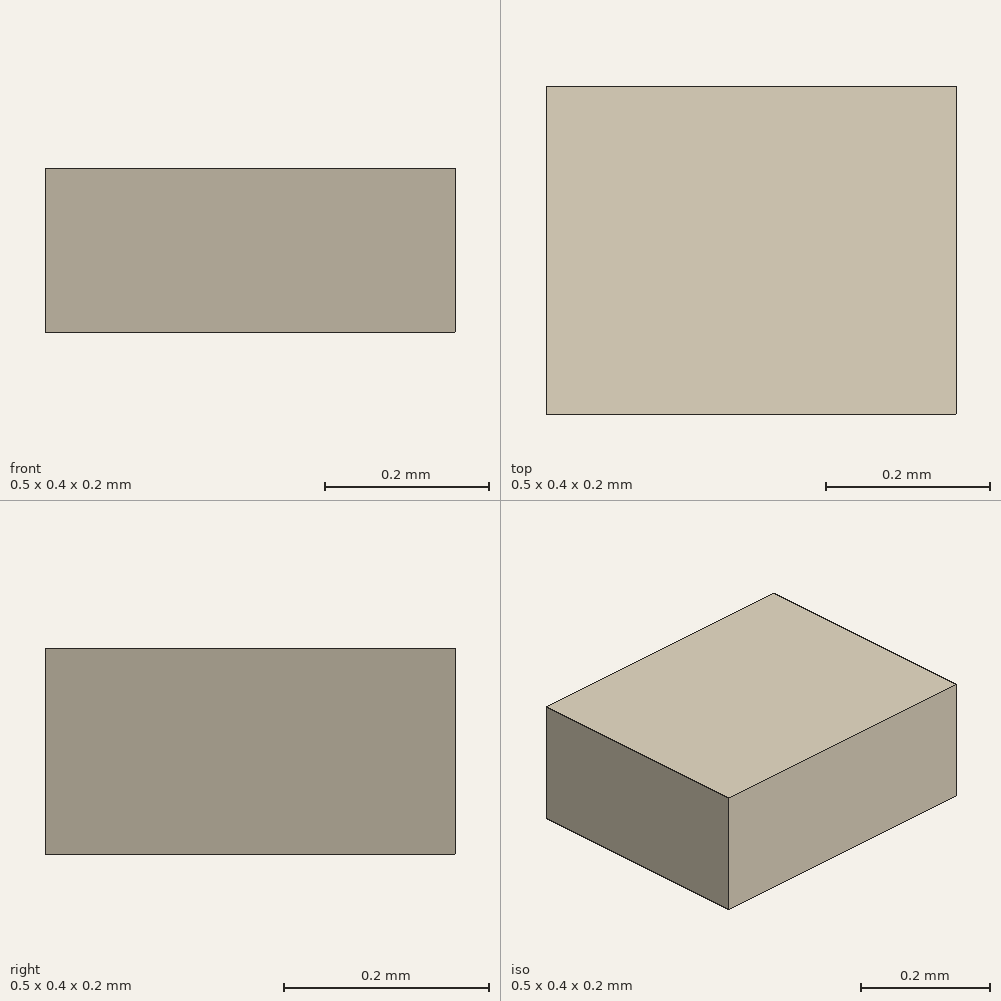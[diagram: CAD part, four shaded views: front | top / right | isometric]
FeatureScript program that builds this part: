
annotation { "Feature Type Name" : "Feature", "Feature Type Description" : "" }
export const myFeature = defineFeature(function(context is Context, id is Id, definition is map)
    precondition{}
    {
        {
            var Q0;
            Q0=qCreatedBy(makeId("Top.planeOp"),FACE);
            var sketch = newSketch(context, id + "F0", { "sketchPlane" : qUnion([Q0])});
            skCircle(sketch, "E0", {"center": v(0, 0) * mm, "radius": 2.54 * mm});
            skLineSegment(sketch, "E1", {"start": v(0, 0) * mm, "end": v(-3.04, 3.04) * mm});
            skPoint(sketch, "E2", {"position": v(-1.8, 1.8) * mm});
            skSolve(sketch);
        }
        {
            var Q0;
            Q0=qCreatedBy(makeId("Top.planeOp"),FACE);
            var sketch = newSketch(context, id + "F1", { "sketchPlane" : qUnion([Q0])});
            skLineSegment(sketch, "E3.bottom", {"start": v(-1, 1) * mm, "end": v(1, 1) * mm});
            skLineSegment(sketch, "E3.top", {"start": v(-1, -1) * mm, "end": v(1, -1) * mm});
            skLineSegment(sketch, "E3.left", {"start": v(-1, 1) * mm, "end": v(-1, -1) * mm});
            skLineSegment(sketch, "E3.right", {"start": v(1, 1) * mm, "end": v(1, -1) * mm});
            skPoint(sketch, "E3.middle", {"position": v(0, 0) * mm});
            skLineSegment(sketch, "E4.bottom", {"start": v(-1, 1) * mm, "end": v(-0.5, 1) * mm});
            skLineSegment(sketch, "E4.top", {"start": v(-1, 0.6) * mm, "end": v(-0.5, 0.6) * mm});
            skLineSegment(sketch, "E4.left", {"start": v(-1, 1) * mm, "end": v(-1, 0.6) * mm});
            skLineSegment(sketch, "E4.right", {"start": v(-0.5, 1) * mm, "end": v(-0.5, 0.6) * mm});
            skLineSegment(sketch, "E5.0.1.0", {"start": v(-1, -0.2) * mm, "end": v(-0.5, -0.2) * mm});
            skLineSegment(sketch, "E5.0.1.1", {"start": v(-0.5, 0.2) * mm, "end": v(-0.5, -0.2) * mm});
            skLineSegment(sketch, "E5.0.1.2", {"start": v(-1, 0.2) * mm, "end": v(-0.5, 0.2) * mm});
            skLineSegment(sketch, "E5.0.1.3", {"start": v(-1, 0.2) * mm, "end": v(-1, -0.2) * mm});
            skLineSegment(sketch, "E5.0.2.0", {"start": v(-1, -1) * mm, "end": v(-0.5, -1) * mm});
            skLineSegment(sketch, "E5.0.2.1", {"start": v(-0.5, -0.6) * mm, "end": v(-0.5, -1) * mm});
            skLineSegment(sketch, "E5.0.2.2", {"start": v(-1, -0.6) * mm, "end": v(-0.5, -0.6) * mm});
            skLineSegment(sketch, "E5.0.2.3", {"start": v(-1, -0.6) * mm, "end": v(-1, -1) * mm});
            skLineSegment(sketch, "E5.direction1", {"start": v(-1, 0.6) * mm, "end": v(24, 0.6) * mm, "construction": true});
            skLineSegment(sketch, "E5.direction2", {"start": v(-1, 0.6) * mm, "end": v(-1, -0.2) * mm, "construction": true});
            skSolve(sketch);
        }
        {
            var Q0;
            Q0=makeQuery(id+"F1.imprint","IMPRINT",FACE,{"disambiguationData":[TD([[makeQuery(id+"F1.imprint","IMPRINT",EDGE,{"derivedFrom":sQuery(id+"F1.wireOp",EDGE,"E4.bottom")}),-1.0]])]});
            var Q1;
            Q1=makeQuery(id+"F1.imprint","IMPRINT",FACE,{"disambiguationData":[TD([[makeQuery(id+"F1.imprint","IMPRINT",EDGE,{"derivedFrom":sQuery(id+"F1.wireOp",EDGE,"E5.0.1.0")}),1.0]])]});
            var Q2;
            Q2=makeQuery(id+"F1.imprint","IMPRINT",FACE,{"disambiguationData":[TD([[makeQuery(id+"F1.imprint","IMPRINT",EDGE,{"derivedFrom":sQuery(id+"F1.wireOp",EDGE,"E5.0.2.0")}),1.0]])]});
            var Q3;
            Q3=sQuery(id+"F1.wireOp",EDGE,"E4.bottom");
            var Q4;
            Q4=sQuery(id+"F1.wireOp",EDGE,"E4.left");
            var Q5;
            Q5=sQuery(id+"F1.wireOp",EDGE,"E4.top");
            var Q6;
            Q6=sQuery(id+"F1.wireOp",EDGE,"E4.right");
            var Q7;
            Q7=sQuery(id+"F1.wireOp",EDGE,"E5.0.1.2");
            var Q8;
            Q8=sQuery(id+"F1.wireOp",EDGE,"E5.0.1.3");
            var Q9;
            Q9=sQuery(id+"F1.wireOp",EDGE,"E5.0.1.0");
            var Q10;
            Q10=sQuery(id+"F1.wireOp",EDGE,"E5.0.1.1");
            var Q11;
            Q11=sQuery(id+"F1.wireOp",EDGE,"E5.0.2.2");
            var Q12;
            Q12=sQuery(id+"F1.wireOp",EDGE,"E5.0.2.0");
            var Q13;
            Q13=sQuery(id+"F1.wireOp",EDGE,"E5.0.2.1");
            var Q14;
            Q14=sQuery(id+"F1.wireOp",EDGE,"E5.0.2.3");
            extrude(context, id + "F2", {"entities" : qUnion([Q0, Q1, Q2]), "surfaceOperationType" : NewSurfaceOperationType.ADD, "surfaceEntities" : qUnion([Q3, Q4, Q5, Q6, Q7, Q8, Q9, Q10, Q11, Q12, Q13, Q14]), "depth" : .2 * mm, "offsetDistance" : 25 * mm});
        }
    });
